# Revit family: Haworth_Bowi_Chair_Seminar_AP_PRELIMINARY
name_source: partatom
category: Furniture
revit_build: Autodesk Revit 2018 (Build: 20170223_1515(x64)
units: mm (PartAtom-declared; Revit-internal decimal feet)

## family parameters
Always vertical = Yes
Cut with Voids When Loaded = No
OmniClass Number = 23.40.70.14.64.11
OmniClass Title = Office Furniture
Room Calculation Point = No
Shared = No
Work Plane-Based = No

## types (4) — shared parameters
Actual Depth = 606 mm  [stored 1.98819 ft]
Actual Height = 835 mm
Actual Width = 640 mm  [stored 2.09974 ft]
Assembly Code = E2020200
Back Upholstery Finish = Haworth _ Fabric _ Undecided _ Seating _ Lounge
Casters Finish = Haworth _ Polymer _ Slate
Description = Haworth - Bowi - Seminar Chair
Manufacturer = Haworth
Model = SEBIM
Revision Number = 1
Seat Upholstery Finish = Haworth _ Fabric _ Undecided _ Seating _ Lounge
Size = Verify Final Dim. w/ Haworth
URL = https://www.haworth.com
URL - Product = https://www.haworth.com
Warranty = https://www.haworth.com

## per-type parameters (varying)
| type | Upholstered Back | Upholstered Seat |
| Seminar Chair - without Upholstered | No | No |
| Seminar Chair - with Upholstered Seat | No | Yes |
| Seminar Chair - with Upholstered Back | Yes | No |
| Seminar Chair - with Upholstered | Yes | Yes |

note: [stored X ft] marks values corroborated as IEEE doubles in the binary element streams (Revit-internal decimal feet)

## geometry (parser evidence)
native form markers: Sweep x9
no freeform markers — native parametric forms only
